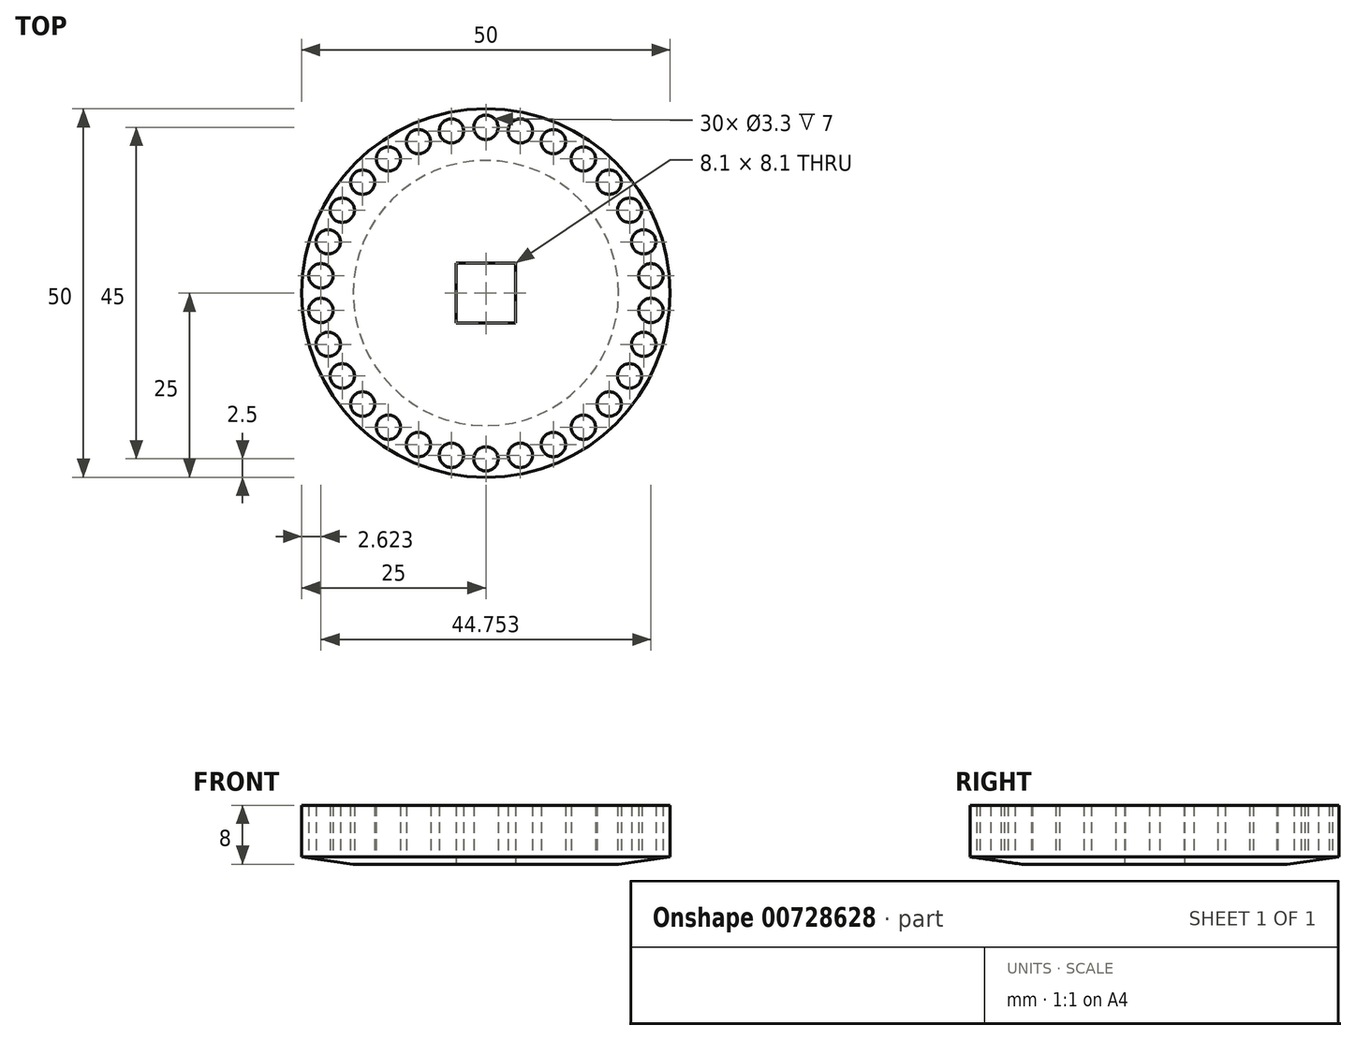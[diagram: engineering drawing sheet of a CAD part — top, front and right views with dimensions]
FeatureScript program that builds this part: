
annotation { "Feature Type Name" : "Feature", "Feature Type Description" : "" }
export const myFeature = defineFeature(function(context is Context, id is Id, definition is map)
    precondition{}
    {
        {
            var Q0;
            Q0=qCreatedBy(makeId("Front.planeOp"),FACE);
            var sketch = newSketch(context, id + "F0", { "sketchPlane" : qUnion([Q0])});
            skCircle(sketch, "E0", {"center": v(0, 0) * mm, "radius": 25 * mm});
            skLineSegment(sketch, "E1.bottom", {"start": v(4.05, -4.05) * mm, "end": v(-4.05, -4.05) * mm});
            skLineSegment(sketch, "E1.top", {"start": v(4.05, 4.05) * mm, "end": v(-4.05, 4.05) * mm});
            skLineSegment(sketch, "E1.left", {"start": v(4.05, -4.05) * mm, "end": v(4.05, 4.05) * mm});
            skLineSegment(sketch, "E1.right", {"start": v(-4.05, -4.05) * mm, "end": v(-4.05, 4.05) * mm});
            skSolve(sketch);
        }
        {
            var Q0;
            Q0 = qSketchRegion(id + "F0", true);
            extrude(context, id + "F1", {"entities" : qUnion([Q0]), "depth" : 8 * mm, "offsetDistance" : 25 * mm});
        }
        {
            var Q0;
            Q0=makeQuery(id+"F1.opExtrude","CAP_FACE",FACE,{"disambiguationData":[OSD([sQuery(id+"F0.wireOp",EDGE,"E0"),sQuery(id+"F0.wireOp",EDGE,"w1h25GKl-cQ8m-VN3m-D3ZC-5HmSG8QwjrAd")])],"isStart":false});
            var sketch = newSketch(context, id + "F2", { "sketchPlane" : qUnion([Q0])});
            skCircle(sketch, "E2", {"center": v(0, 22.5) * mm, "radius": 1.65 * mm});
            skCircle(sketch, "E3.1.0", {"center": v(-4.68, 22) * mm, "radius": 1.65 * mm});
            skCircle(sketch, "E3.2.0", {"center": v(-9.15, 20.55) * mm, "radius": 1.65 * mm});
            skCircle(sketch, "E3.3.0", {"center": v(-13.23, 18.2) * mm, "radius": 1.65 * mm});
            skCircle(sketch, "E3.4.0", {"center": v(-16.72, 15.06) * mm, "radius": 1.65 * mm});
            skCircle(sketch, "E3.5.0", {"center": v(-19.49, 11.25) * mm, "radius": 1.65 * mm});
            skCircle(sketch, "E3.6.0", {"center": v(-21.4, 6.95) * mm, "radius": 1.65 * mm});
            skCircle(sketch, "E3.7.0", {"center": v(-22.38, 2.35) * mm, "radius": 1.65 * mm});
            skCircle(sketch, "E3.8.0", {"center": v(-22.38, -2.35) * mm, "radius": 1.65 * mm});
            skCircle(sketch, "E3.9.0", {"center": v(-21.4, -6.95) * mm, "radius": 1.65 * mm});
            skCircle(sketch, "E3.10.0", {"center": v(-19.49, -11.25) * mm, "radius": 1.65 * mm});
            skCircle(sketch, "E3.11.0", {"center": v(-16.72, -15.06) * mm, "radius": 1.65 * mm});
            skCircle(sketch, "E3.12.0", {"center": v(-13.23, -18.2) * mm, "radius": 1.65 * mm});
            skCircle(sketch, "E3.13.0", {"center": v(-9.15, -20.55) * mm, "radius": 1.65 * mm});
            skCircle(sketch, "E3.14.0", {"center": v(-4.68, -22) * mm, "radius": 1.65 * mm});
            skCircle(sketch, "E3.15.0", {"center": v(0, -22.5) * mm, "radius": 1.65 * mm});
            skCircle(sketch, "E3.16.0", {"center": v(4.68, -22) * mm, "radius": 1.65 * mm});
            skCircle(sketch, "E3.17.0", {"center": v(9.15, -20.55) * mm, "radius": 1.65 * mm});
            skCircle(sketch, "E3.18.0", {"center": v(13.23, -18.2) * mm, "radius": 1.65 * mm});
            skCircle(sketch, "E3.19.0", {"center": v(16.72, -15.06) * mm, "radius": 1.65 * mm});
            skPoint(sketch, "E3.center", {"position": v(0, 0) * mm});
            skCircle(sketch, "E4.1.20.0", {"center": v(19.49, -11.25) * mm, "radius": 1.65 * mm});
            skCircle(sketch, "E4.1.21.0", {"center": v(21.4, -6.95) * mm, "radius": 1.65 * mm});
            skCircle(sketch, "E4.1.22.0", {"center": v(22.38, -2.35) * mm, "radius": 1.65 * mm});
            skCircle(sketch, "E4.1.23.0", {"center": v(22.38, 2.35) * mm, "radius": 1.65 * mm});
            skCircle(sketch, "E4.1.24.0", {"center": v(21.4, 6.95) * mm, "radius": 1.65 * mm});
            skCircle(sketch, "E5.1.25.0", {"center": v(19.49, 11.25) * mm, "radius": 1.65 * mm});
            skCircle(sketch, "E5.1.26.0", {"center": v(16.72, 15.06) * mm, "radius": 1.65 * mm});
            skCircle(sketch, "E5.1.27.0", {"center": v(13.23, 18.2) * mm, "radius": 1.65 * mm});
            skCircle(sketch, "E5.1.28.0", {"center": v(9.15, 20.55) * mm, "radius": 1.65 * mm});
            skCircle(sketch, "E5.1.29.0", {"center": v(4.68, 22) * mm, "radius": 1.65 * mm});
            skSolve(sketch);
        }
        {
            var Q0;
            Q0 = qSketchRegion(id + "F2", true);
            extrude(context, id + "F3", {"entities" : qUnion([Q0]), "operationType" : NewBodyOperationType.REMOVE, "depth" : 10 * mm, "offsetDistance" : 25 * mm, "hasSecondDirection" : true, "secondDirectionOppositeDirection" : true, "secondDirectionDepth" : 7 * mm});
        }
        {
            var Q0;
            Q0=makeQuery(id+"F1.opExtrude","CAP_EDGE",EDGE,{"disambiguationData":[OSD([sQuery(id+"F0.wireOp",EDGE,"E0")])],"isStart":true});
            chamfer(context, id + "F4", {"entities" : qUnion([Q0]), "chamferType" : ChamferType.TWO_OFFSETS, "width1" : 1 * mm, "oppositeDirection" : false, "width2" : 7 * mm, "tangentPropagation" : true});
        }
        {
            var Q0;
            Q0=makeQuery(id+"F1.opExtrude","SWEPT_BODY",BODY,{"disambiguationData":[OSD([sQuery(id+"F0.wireOp",EDGE,"E0"),sQuery(id+"F0.wireOp",EDGE,"E1.bottom"),sQuery(id+"F0.wireOp",EDGE,"E1.top"),sQuery(id+"F0.wireOp",EDGE,"E1.left"),sQuery(id+"F0.wireOp",EDGE,"E1.right")])]});
            var Q1;
            Q1=makeQuery(id+"F1.opExtrude","CAP_EDGE",EDGE,{"disambiguationData":[OSD([sQuery(id+"F0.wireOp",EDGE,"E1.top")])],"isStart":false});
            transform(context, id + "F5", {"entities" : qUnion([Q0]), "transformType" : TransformType.ROTATION, "transformAxis" : qUnion([Q1]), "angle" : 90 * degree, "makeCopy" : false});
        }
    });
